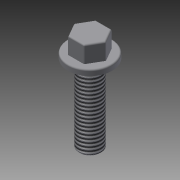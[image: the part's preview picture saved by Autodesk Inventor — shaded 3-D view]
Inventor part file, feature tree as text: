
AUTODESK INVENTOR PART (.ipt)
format: ipt  version: 2015 (Build 190159000, 159)  size: 128,512 bytes
history: native  units: mm
features: extrude x3, sketch x3, fillet x1, thread x1, chamfer x1
ambient origin geometry x8: Origin, YZ Plane, XZ Plane, XY Plane, X Axis, Y Axis, Z Axis, Center Point
bodies: 实体1 (feature_tree)
feature tree (9):
  extrude  "拉伸1"  Depth=2.0mm TaperAngle=0.0deg
  extrude  "拉伸2"  Depth=10.0mm
  fillet  "圆角1"  Radius=6.0mm
  extrude  "拉伸3"  Depth=8.0mm
  thread  "螺纹1"  [1 undecoded]
  chamfer  "倒角1"  Distance=10.0mm
  sketch  "草图1"  dims[d0=16.0mm d1=2.0mm d2=0.0mm]
  sketch  "草图2"  dims[d3=2.76768mm d4=10.0mm d5=6.0mm d6=0.0mm]
  sketch  "草图3"  dims[d7=0.5mm d8=8.0mm d9=28.0mm d10=0.0mm d11=10.0mm d12=0.0mm d13=0.5mm d14=2.0mm d15=45.0deg]
note: 1 required parameter value undecoded (feature->parameter linkage not recoverable at this tier; creation-order binding heuristic only, values carry confidence <= 0.55)
